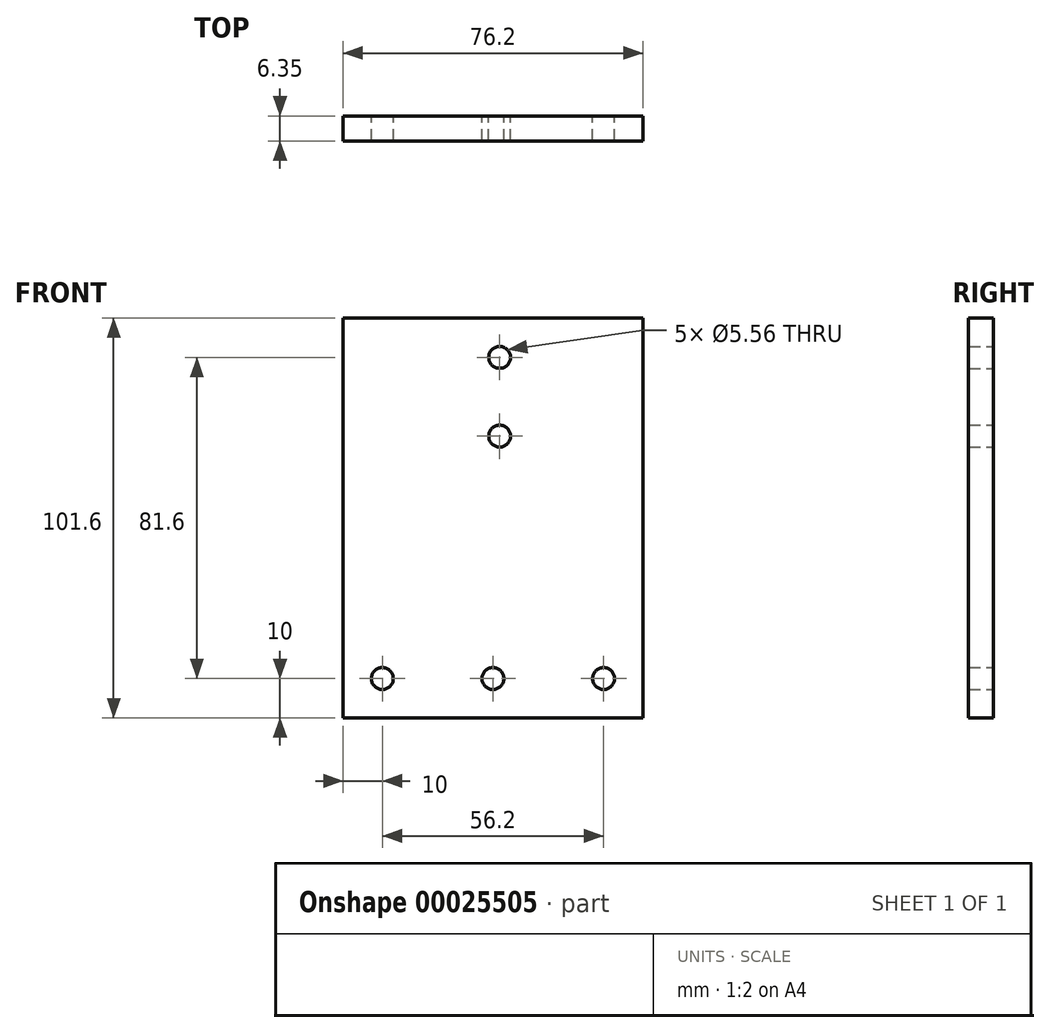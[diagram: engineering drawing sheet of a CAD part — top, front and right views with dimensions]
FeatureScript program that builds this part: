
annotation { "Feature Type Name" : "Feature", "Feature Type Description" : "" }
export const myFeature = defineFeature(function(context is Context, id is Id, definition is map)
    precondition{}
    {
        {
            var Q0;
            Q0=qCreatedBy(makeId("Front.planeOp"),FACE);
            var sketch = newSketch(context, id + "F0", { "sketchPlane" : qUnion([Q0])});
            skLineSegment(sketch, "E0.bottom", {"start": v(-38.1, -10) * mm, "end": v(38.1, -10) * mm});
            skLineSegment(sketch, "E0.top", {"start": v(-38.1, 91.6) * mm, "end": v(38.1, 91.6) * mm});
            skLineSegment(sketch, "E0.left", {"start": v(-38.1, -10) * mm, "end": v(-38.1, 91.6) * mm});
            skLineSegment(sketch, "E0.right", {"start": v(38.1, -10) * mm, "end": v(38.1, 91.6) * mm});
            skCircle(sketch, "E1", {"center": v(0, 0) * mm, "radius": 2.78 * mm});
            skCircle(sketch, "E2", {"center": v(-28.1, 0) * mm, "radius": 2.78 * mm});
            skCircle(sketch, "E3", {"center": v(28.1, 0) * mm, "radius": 2.78 * mm});
            skCircle(sketch, "E4", {"center": v(1.7, 61.6) * mm, "radius": 2.78 * mm});
            skCircle(sketch, "E5", {"center": v(1.7, 81.6) * mm, "radius": 2.78 * mm});
            skLineSegment(sketch, "E6", {"start": v(-28.1, 0) * mm, "end": v(28.1, 0) * mm, "construction": true});
            skPoint(sketch, "E7", {"position": v(0, -10) * mm});
            skSolve(sketch);
        }
        {
            var Q0;
            Q0=makeQuery(id+"F0.imprint","IMPRINT",FACE,{"disambiguationData":[TD([[makeQuery(id+"F0.imprint","IMPRINT",EDGE,{"derivedFrom":sQuery(id+"F0.wireOp",EDGE,"E0.bottom")}),1.0]])]});
            extrude(context, id + "F1", {"entities" : qUnion([Q0]), "depth" : 6.35 * mm});
        }
    });
